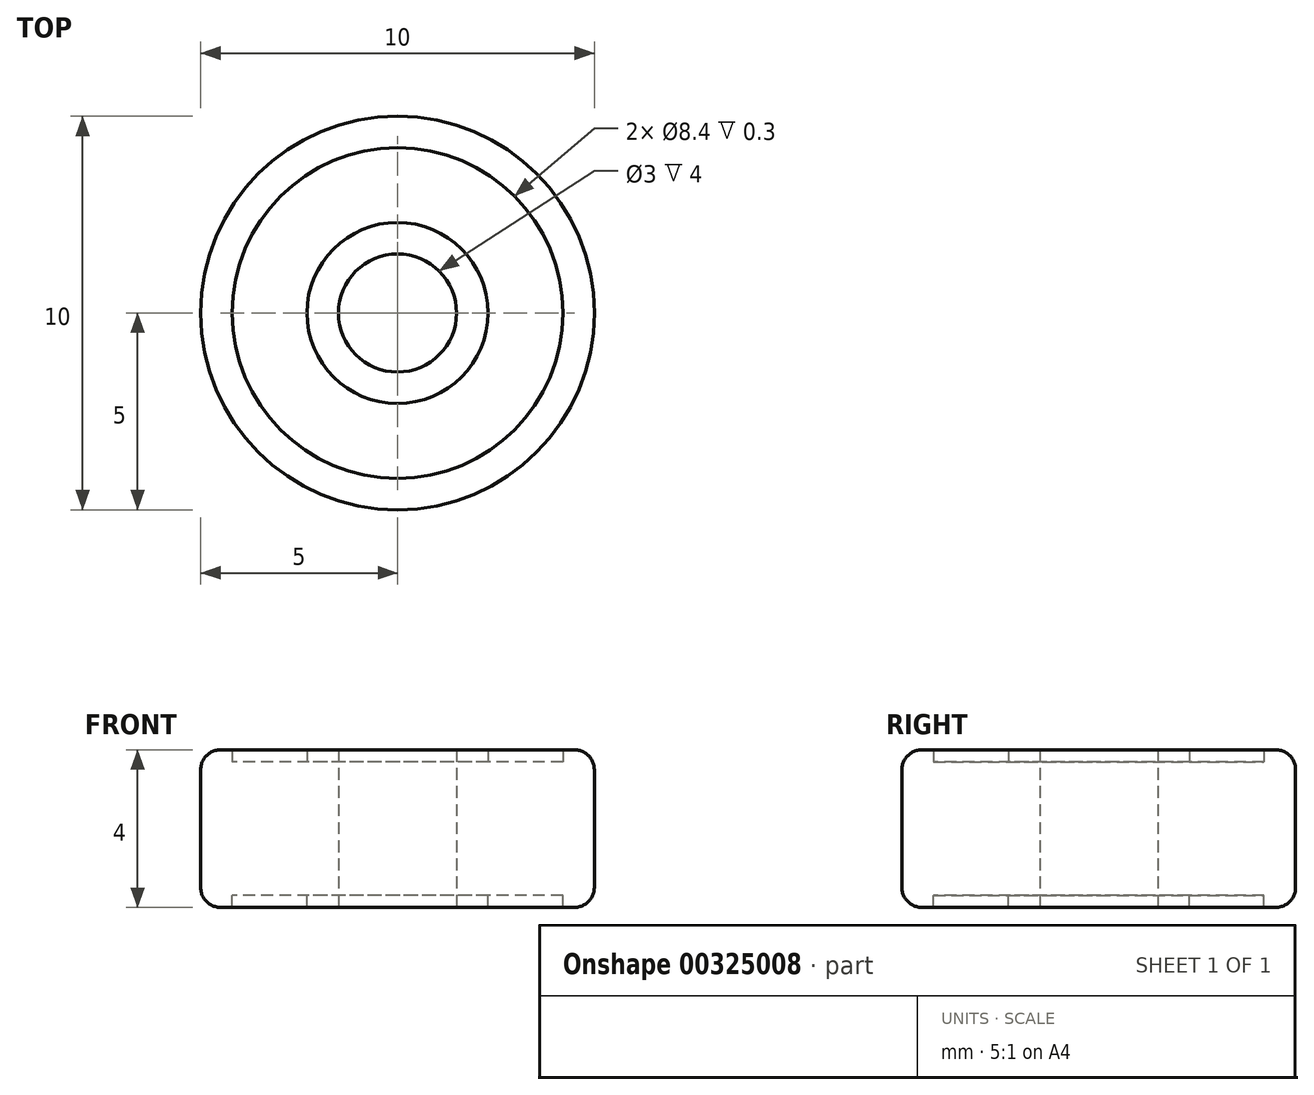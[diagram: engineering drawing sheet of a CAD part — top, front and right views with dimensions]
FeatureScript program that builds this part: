
annotation { "Feature Type Name" : "Feature", "Feature Type Description" : "" }
export const myFeature = defineFeature(function(context is Context, id is Id, definition is map)
    precondition{}
    {
        {
            var Q0;
            Q0=qCreatedBy(makeId("Top.planeOp"),FACE);
            var sketch = newSketch(context, id + "F0", { "sketchPlane" : qUnion([Q0])});
            skCircle(sketch, "E0", {"center": v(0, 0) * mm, "radius": 1.5 * mm});
            skCircle(sketch, "E1", {"center": v(0, 0) * mm, "radius": 5 * mm});
            skCircle(sketch, "E2", {"center": v(0, 0) * mm, "radius": 2.3 * mm});
            skCircle(sketch, "E3", {"center": v(0, 0) * mm, "radius": 4.2 * mm});
            skSolve(sketch);
        }
        {
            var Q0;
            Q0=makeQuery(id+"F0.imprint","IMPRINT",FACE,{"disambiguationData":[TD([[makeQuery(id+"F0.imprint","IMPRINT",EDGE,{"derivedFrom":sQuery(id+"F0.wireOp",EDGE,"E1")}),1.0]])]});
            extrude(context, id + "F1", {"entities" : qUnion([Q0]), "depth" : 3.5 * mm});
        }
        {
            var Q0;
            Q0=makeQuery(id+"F0.imprint","IMPRINT",FACE,{"disambiguationData":[TD([[makeQuery(id+"F0.imprint","IMPRINT",EDGE,{"derivedFrom":sQuery(id+"F0.wireOp",EDGE,"E2")}),-1.0]])]});
            extrude(context, id + "F2", {"entities" : qUnion([Q0]), "operationType" : NewBodyOperationType.ADD, "depth" : 3.2 * mm});
        }
        {
            var Q0;
            Q0=makeQuery(id+"F0.imprint","IMPRINT",FACE,{"disambiguationData":[TD([[makeQuery(id+"F0.imprint","IMPRINT",EDGE,{"derivedFrom":sQuery(id+"F0.wireOp",EDGE,"E0")}),-1.0]])]});
            extrude(context, id + "F3", {"entities" : qUnion([Q0]), "operationType" : NewBodyOperationType.ADD, "depth" : 3.5 * mm});
        }
        {
            var Q0;
            Q0=makeQuery(id+"F0.imprint","IMPRINT",FACE,{"disambiguationData":[TD([[makeQuery(id+"F0.imprint","IMPRINT",EDGE,{"derivedFrom":sQuery(id+"F0.wireOp",EDGE,"E1")}),1.0]])]});
            extrude(context, id + "F4", {"entities" : qUnion([Q0]), "operationType" : NewBodyOperationType.ADD, "oppositeDirection" : true, "depth" : .5 * mm});
        }
        {
            var Q0;
            Q0=makeQuery(id+"F0.imprint","IMPRINT",FACE,{"disambiguationData":[TD([[makeQuery(id+"F0.imprint","IMPRINT",EDGE,{"derivedFrom":sQuery(id+"F0.wireOp",EDGE,"E0")}),-1.0]])]});
            extrude(context, id + "F5", {"entities" : qUnion([Q0]), "operationType" : NewBodyOperationType.ADD, "oppositeDirection" : true, "depth" : .5 * mm});
        }
        {
            var Q0;
            Q0=makeQuery(id+"F0.imprint","IMPRINT",FACE,{"disambiguationData":[TD([[makeQuery(id+"F0.imprint","IMPRINT",EDGE,{"derivedFrom":sQuery(id+"F0.wireOp",EDGE,"E2")}),-1.0]])]});
            extrude(context, id + "F6", {"entities" : qUnion([Q0]), "operationType" : NewBodyOperationType.ADD, "oppositeDirection" : true, "depth" : .2 * mm});
        }
        {
            var Q0;
            Q0=makeQuery(id+"F1.opExtrude","CAP_EDGE",EDGE,{"disambiguationData":[OSD([sQuery(id+"F0.wireOp",EDGE,"E1")])],"isStart":false});
            var Q1;
            Q1=makeQuery(id+"F4.opExtrude","CAP_EDGE",EDGE,{"disambiguationData":[OSD([sQuery(id+"F0.wireOp",EDGE,"E1")])],"isStart":false});
            fillet(context, id + "F7", {"entities" : qUnion([Q0, Q1]), "radius" : .5 * mm, "tangentPropagation" : true, "allowEdgeOverflow" : false});
        }
    });
